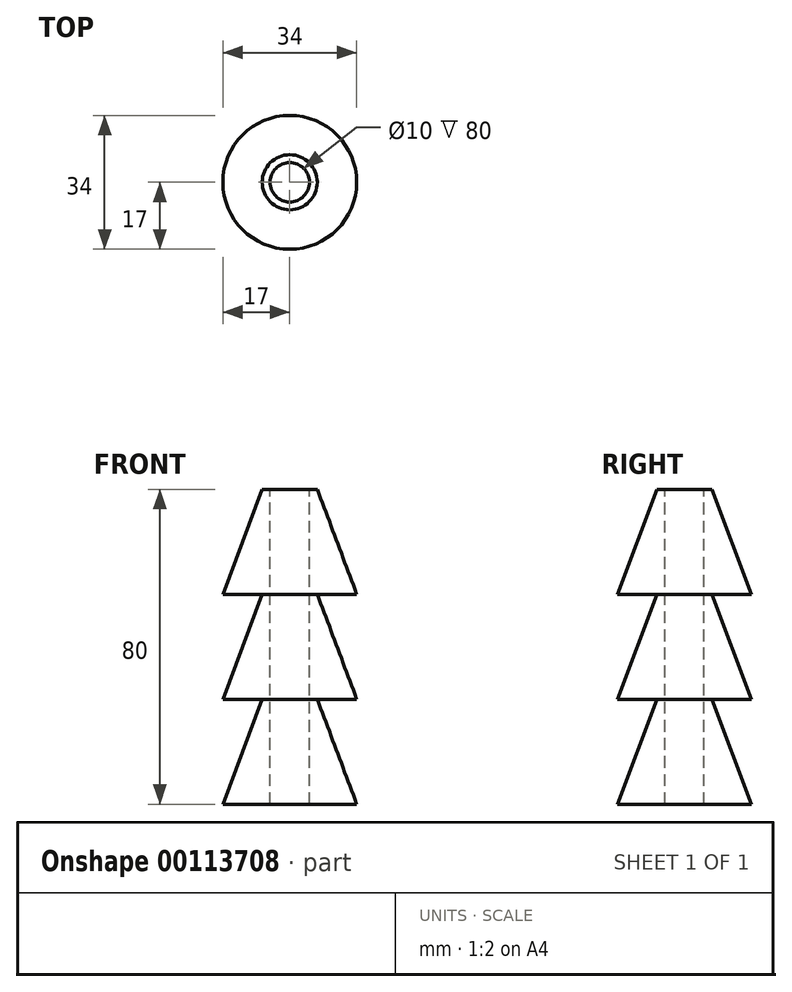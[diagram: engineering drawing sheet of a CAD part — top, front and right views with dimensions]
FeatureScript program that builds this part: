
annotation { "Feature Type Name" : "Feature", "Feature Type Description" : "" }
export const myFeature = defineFeature(function(context is Context, id is Id, definition is map)
    precondition{}
    {
        {
            var Q0;
            Q0=qCreatedBy(makeId("Front.planeOp"),FACE);
            var sketch = newSketch(context, id + "F0", { "sketchPlane" : qUnion([Q0])});
            skLineSegment(sketch, "E0.bottom", {"start": v(5, 40) * mm, "end": v(-5, 40) * mm, "construction": true});
            skLineSegment(sketch, "E0.top", {"start": v(5, -40) * mm, "end": v(-5, -40) * mm, "construction": true});
            skLineSegment(sketch, "E0.left", {"start": v(5, 40) * mm, "end": v(5, -40) * mm, "construction": true});
            skLineSegment(sketch, "E0.right", {"start": v(-5, 40) * mm, "end": v(-5, -40) * mm, "construction": true});
            skPoint(sketch, "E0.middle", {"position": v(0, 0) * mm});
            skLineSegment(sketch, "E1", {"start": v(0, 40) * mm, "end": v(0, -40) * mm, "construction": true});
            skLineSegment(sketch, "E2.bottom", {"start": v(7, 40) * mm, "end": v(-7, 40) * mm, "construction": true});
            skLineSegment(sketch, "E2.top", {"start": v(7, -40) * mm, "end": v(-7, -40) * mm, "construction": true});
            skLineSegment(sketch, "E2.left", {"start": v(7, 40) * mm, "end": v(7, -40) * mm, "construction": true});
            skLineSegment(sketch, "E2.right", {"start": v(-7, 40) * mm, "end": v(-7, -40) * mm, "construction": true});
            skLineSegment(sketch, "E3", {"start": v(-17, 13.33) * mm, "end": v(7, 13.33) * mm, "construction": true});
            skLineSegment(sketch, "E4", {"start": v(-17, -13.33) * mm, "end": v(7, -13.33) * mm, "construction": true});
            skLineSegment(sketch, "E5.0", {"start": v(-17, 40) * mm, "end": v(-17, -40) * mm, "construction": true});
            skLineSegment(sketch, "E6", {"start": v(-7, 40) * mm, "end": v(-17, 13.33) * mm});
            skLineSegment(sketch, "E7", {"start": v(-7, 13.33) * mm, "end": v(-17, -13.33) * mm});
            skLineSegment(sketch, "E8", {"start": v(-7, -13.33) * mm, "end": v(-17, -40) * mm});
            skLineSegment(sketch, "E9", {"start": v(-17, -13.33) * mm, "end": v(-7, -13.33) * mm});
            skLineSegment(sketch, "E10", {"start": v(-17, 13.33) * mm, "end": v(-7, 13.33) * mm});
            skLineSegment(sketch, "E11", {"start": v(-17, -40) * mm, "end": v(0, -40) * mm});
            skLineSegment(sketch, "E12", {"start": v(0, 40) * mm, "end": v(0, -40) * mm});
            skLineSegment(sketch, "E13", {"start": v(0, 40) * mm, "end": v(-7, 40) * mm});
            skLineSegment(sketch, "E14.bottom", {"start": v(-7, -40) * mm, "end": v(6.54, -40) * mm});
            skSolve(sketch);
        }
        {
            var Q0;
            Q0=makeQuery(id+"F0.imprint","IMPRINT",FACE,{"disambiguationData":[TD([[makeQuery(id+"F0.imprint","IMPRINT",EDGE,{"derivedFrom":sQuery(id+"F0.wireOp",EDGE,"E6")}),1.0]])]});
            var Q1;
            Q1=sQuery(id+"F0.wireOp",EDGE,"E12");
            revolve(context, id + "F1", {"entities" : qUnion([Q0]), "axis" : qUnion([Q1]), "revolveType" : RevolveType.FULL});
        }
        {
            var Q0;
            Q0=makeQuery(id+"F1.opRevolve","SWEPT_FACE",FACE,{"disambiguationData":[OSD([sQuery(id+"F0.wireOp",EDGE,"E13")])]});
            var sketch = newSketch(context, id + "F2", { "sketchPlane" : qUnion([Q0])});
            skCircle(sketch, "E15", {"center": v(0, 0) * mm, "radius": 5 * mm});
            skSolve(sketch);
        }
        {
            var Q0;
            Q0=makeQuery(id+"F2.imprint","IMPRINT",FACE,{"disambiguationData":[TD([[makeQuery(id+"F2.imprint","IMPRINT",EDGE,{"derivedFrom":sQuery(id+"F2.wireOp",EDGE,"E15")}),1.0]])]});
            extrude(context, id + "F3", {"entities" : qUnion([Q0]), "operationType" : NewBodyOperationType.REMOVE, "endBound" : BoundingType.THROUGH_ALL, "oppositeDirection" : true, "depth" : 25 * mm});
        }
    });
